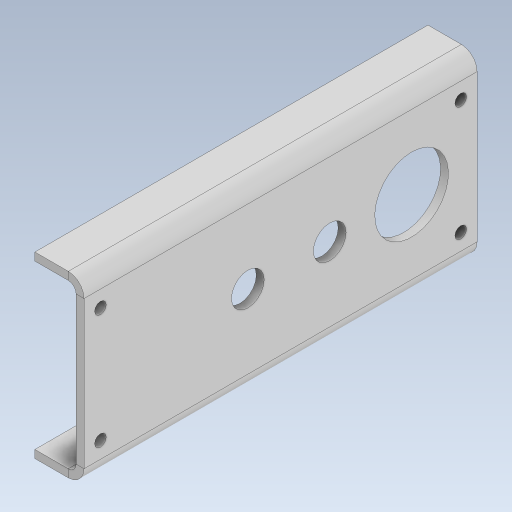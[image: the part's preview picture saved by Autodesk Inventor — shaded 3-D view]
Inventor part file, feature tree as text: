
AUTODESK INVENTOR PART (.ipt)
format: ipt  version: 2023 (Build 270158000, 158)  size: 161,280 bytes
history: native  units: in
note: dims shown in document units (in); Inventor stores cm internally (conversion verified against a paired STEP export)
features: sheet_metal_op x4, sketch x2, other x2
ambient origin geometry x8: Origin, YZ Plane, XZ Plane, XY Plane, X Axis, Y Axis, Z Axis, Center Point
bodies: Body1 (feature_tree)
feature tree (8):
  sheet_metal_op  "Face2"
  sheet_metal_op  "Flange1"
  sketch  "Sketch1"  dims[d0=2.25in]
  other  "Plate2"
  sketch  "Sketch2"  dims[d1=6.0in d3=1.25in d4=1.25in d5=1.0in d7=0.5in d8=1.125in d10=0.12in d11=0.177in d12=5.5in d13=1.75in d14=0.5in d15=6.0in d16=0.5in d17=6.0in d18=0.12in d19=0.06in d20=0.24in d21=0.12in d22=0.75in d23=90.0deg d24=0.12in d25=0.48in d26=0.12in d27=0.12in]
  other  "Plate3"
  sheet_metal_op  "Bend1"
  sheet_metal_op  "Corner1"
